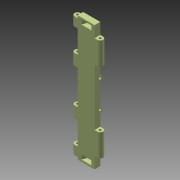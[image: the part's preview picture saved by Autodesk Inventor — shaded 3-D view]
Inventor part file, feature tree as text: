
AUTODESK INVENTOR PART (.ipt)
format: ipt  version: 2015 (Build 190159000, 159)  size: 436,224 bytes
history: native  units: mm
features: extrude x13, sketch x13, pattern_linear x5, thread x4, fillet x2, plane x1
ambient origin geometry x8: Origin, YZ Plane, XZ Plane, XY Plane, X Axis, Y Axis, Z Axis, Center Point
bodies: 实体1 (feature_tree)
feature tree (38):
  extrude  "拉伸1"  Depth=25.0mm
  extrude  "拉伸2"  Depth=550.0mm
  extrude  "拉伸3"  Depth=50.0mm
  pattern_linear  "矩形阵列1"  Count1=2 Spacing1=0.0mm
  extrude  "拉伸4"  Depth=10.0mm
  pattern_linear  "矩形阵列2"  Count1=6 Spacing1=0.0mm
  extrude  "拉伸5"  TaperAngle=45.0deg  [1 undecoded]
  extrude  "拉伸6"  Depth=10.0mm TaperAngle=0.0deg
  pattern_linear  "矩形阵列3"  Count1=8  [1 undecoded]
  extrude  "拉伸7"  Depth=10.0mm
  extrude  "拉伸8"  Depth=10.0mm
  extrude  "拉伸9"  Depth=40.0mm
  thread  "螺纹1"  [1 undecoded]
  thread  "螺纹2"  [1 undecoded]
  thread  "螺纹3"  [1 undecoded]
  thread  "螺纹4"  [1 undecoded]
  pattern_linear  "矩形阵列4"  Spacing1=3.0mm  [1 undecoded]
  extrude  "拉伸10"  Depth=25.0mm
  extrude  "拉伸11"  Depth=25.0mm
  plane  "工作平面1"
  extrude  "拉伸12"  Depth=25.0mm
  fillet  "圆角1"  Radius=8.0mm
  fillet  "圆角2"  Radius=5.0mm
  pattern_linear  "矩形阵列5"  Spacing1=5.0mm  [1 undecoded]
  extrude  "拉伸13"  Depth=5.0mm
  sketch  "草图1"  dims[d0=75.0mm d1=25.0mm]
  sketch  "草图2"  dims[d2=550.0mm d3=0.0mm d4=480.0mm]
  sketch  "草图3"  dims[d5=50.0mm d6=15.0mm]
  sketch  "草图4"  dims[d7=35.0mm d8=20.0mm d9=0.0mm]
  sketch  "草图5"  dims[d10=23.561117mm d11=10.0mm d12=60.0mm d13=0.0mm]
  sketch  "草图6"  dims[d14=80.0mm d16=60.0mm d17=45.0deg]
  sketch  "草图7"  dims[d18=10.0mm d19=60.0mm d20=0.0mm d21=80.0mm d23=60.0mm]
  sketch  "草图8"  dims[d24=95.0mm d25=10.0mm]
  sketch  "草图9"  dims[d26=70.0mm d27=0.0mm d28=10.0mm]
  sketch  "草图10"  dims[d29=70.0mm d30=0.0mm d31=40.0mm d33=120.0mm d34=10.0mm d35=550.0mm d36=0.0mm d37=30.0mm d38=80.0mm]
  sketch  "草图11"  dims[d39=5.0mm]
  sketch  "草图12"  dims[d40=5.0mm d41=0.0mm]
  sketch  "草图13"  dims[d42=3.0mm d43=3.0mm d44=3.0mm d45=3.0mm d46=8.0mm d47=8.0mm d48=5.0mm d49=5.0mm d50=5.0mm d51=5.0mm d52=5.0mm d53=5.0mm d54=10.0mm d55=0.0mm d56=10.0mm d57=0.0mm d58=10.0mm d59=0.0mm d60=10.0mm d61=0.0mm d62=10.0mm d63=0.0mm d64=40.0mm d66=120.0mm d67=25.0mm d68=25.0mm d69=10.0mm d70=10.0mm d71=550.0mm d72=0.0mm d73=25.0mm d74=100.0mm d75=150.0mm d76=50.0mm d77=50.0mm d78=100.0mm d79=50.0mm d80=25.0mm d81=0.0mm d82=-10.0mm d83=40.0mm d84=20.0mm d85=15.0mm d86=0.0mm d87=6.0mm d88=4.0mm d89=20.0mm d91=515.0mm d92=10.0mm d93=25.0mm d94=10.0mm d95=25.0mm d96=25.0mm d97=0.0mm]
note: 8 required parameter values undecoded (feature->parameter linkage not recoverable at this tier; creation-order binding heuristic only, values carry confidence <= 0.55)
